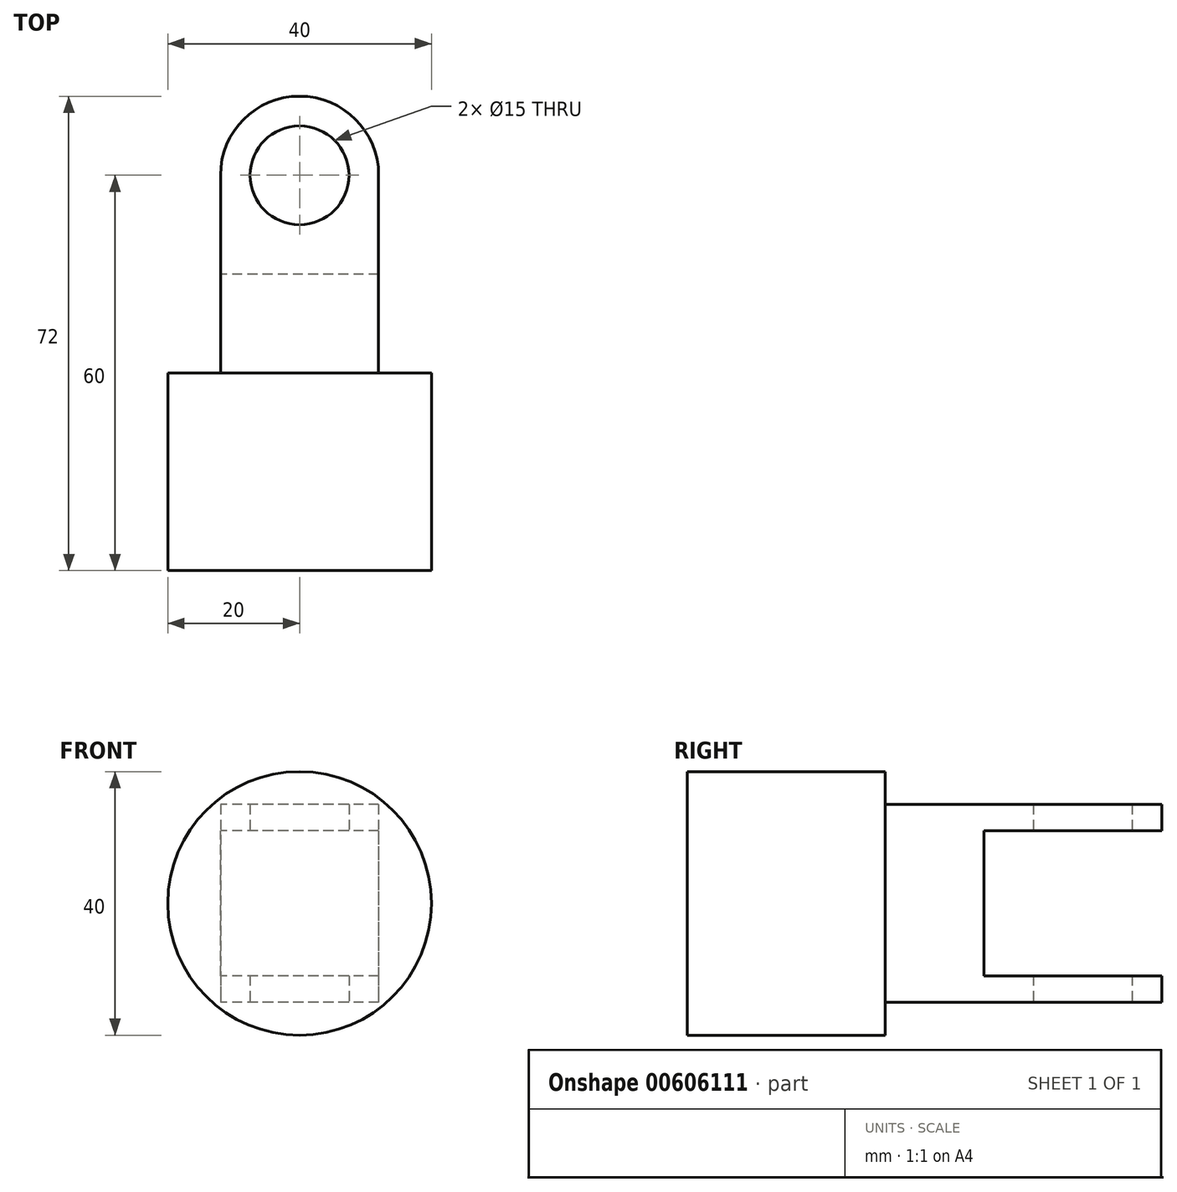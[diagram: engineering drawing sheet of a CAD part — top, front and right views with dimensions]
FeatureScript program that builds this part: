
annotation { "Feature Type Name" : "Feature", "Feature Type Description" : "" }
export const myFeature = defineFeature(function(context is Context, id is Id, definition is map)
    precondition{}
    {
        {
            var Q0;
            Q0=qCreatedBy(makeId("Top.planeOp"),FACE);
            var sketch = newSketch(context, id + "F0", { "sketchPlane" : qUnion([Q0])});
            skLineSegment(sketch, "E0.bottom", {"start": v(12, 15) * mm, "end": v(-12, 15) * mm});
            skLineSegment(sketch, "E0.top", {"start": v(12, -15) * mm, "end": v(-12, -15) * mm});
            skLineSegment(sketch, "E0.left", {"start": v(12, 15) * mm, "end": v(12, -15) * mm});
            skLineSegment(sketch, "E0.right", {"start": v(-12, 15) * mm, "end": v(-12, -15) * mm});
            skPoint(sketch, "E0.middle", {"position": v(0, 0) * mm});
            skCircle(sketch, "E1", {"center": v(0, 15) * mm, "radius": 12 * mm});
            skCircle(sketch, "E2", {"center": v(0, 15) * mm, "radius": 7.5 * mm});
            skSolve(sketch);
        }
        {
            var Q0;
            {var subQ1=sQuery(id+"F0.wireOp",EDGE,"E0.bottom");var subQ3=sQuery(id+"F0.wireOp",EDGE,"E2");var subQ4=makeQuery(id+"F0.imprint","INTERSECT",VERTEX,{"disambiguationData":[OD(0.0)],"derivedFrom":[subQ1,subQ3]});Q0=makeQuery(id+"F0.imprint","IMPRINT",FACE,{"disambiguationData":[TD([[makeQuery(id+"F0.imprint","IMPRINT",EDGE,{"disambiguationData":[TD([[subQ4,-1.0]])],"derivedFrom":subQ3}),-1.0]])]});}
            var Q1;
            {var subQ1=sQuery(id+"F0.wireOp",EDGE,"E0.bottom");var subQ3=sQuery(id+"F0.wireOp",EDGE,"E2");var subQ4=makeQuery(id+"F0.imprint","INTERSECT",VERTEX,{"disambiguationData":[OD(0.0)],"derivedFrom":[subQ1,subQ3]});Q1=makeQuery(id+"F0.imprint","IMPRINT",FACE,{"disambiguationData":[TD([[makeQuery(id+"F0.imprint","IMPRINT",EDGE,{"disambiguationData":[TD([[subQ4,1.0]])],"derivedFrom":subQ3}),-1.0]])]});}
            var Q2;
            Q2=makeQuery(id+"F0.imprint","IMPRINT",FACE,{"disambiguationData":[TD([[makeQuery(id+"F0.imprint","IMPRINT",EDGE,{"derivedFrom":sQuery(id+"F0.wireOp",EDGE,"E0.top")}),-1.0]])]});
            extrude(context, id + "F1", {"entities" : qUnion([Q0, Q1, Q2]), "depth" : 30 * mm, "offsetDistance" : 25.4 * mm});
        }
        {
            var Q0;
            Q0=makeQuery(id+"F1.opExtrude","SWEPT_FACE",FACE,{"disambiguationData":[OSD([sQuery(id+"F0.wireOp",EDGE,"E0.top")])]});
            var sketch = newSketch(context, id + "F2", { "sketchPlane" : qUnion([Q0])});
            skCircle(sketch, "E3", {"center": v(0, 15) * mm, "radius": 20 * mm});
            skPoint(sketch, "E3.centerSnap0", {"position": v(12, 15) * mm});
            skSolve(sketch);
        }
        {
            var Q0;
            Q0=makeQuery(id+"F2.imprint","IMPRINT",FACE,{"disambiguationData":[TD([[makeQuery(id+"F2.imprint","IMPRINT",EDGE,{"derivedFrom":sQuery(id+"F2.wireOp",EDGE,"E3")}),1.0]])]});
            var Q1;
            {var subQ0=sQuery(id+"F0.wireOp",EDGE,"E0.top");Q1=makeQuery(id+"F2.imprint","IMPRINT",FACE,{"disambiguationData":[TD([[makeQuery(id+"F2.imprint","IMPRINT",EDGE,{"derivedFrom":makeQuery(id+"F1.opExtrude","CAP_EDGE",EDGE,{"disambiguationData":[OSD([subQ0])],"isStart":true})}),-1.0]])]});}
            extrude(context, id + "F3", {"entities" : qUnion([Q0, Q1]), "operationType" : NewBodyOperationType.ADD, "depth" : 30 * mm, "offsetDistance" : 25.4 * mm});
        }
        {
            var Q0;
            Q0=makeQuery(id+"F1.opExtrude","SWEPT_FACE",FACE,{"disambiguationData":[OSD([sQuery(id+"F0.wireOp",EDGE,"E0.right")])]});
            var sketch = newSketch(context, id + "F4", { "sketchPlane" : qUnion([Q0])});
            skLineSegment(sketch, "E4.bottom", {"start": v(0, 4) * mm, "end": v(-30, 4) * mm});
            skLineSegment(sketch, "E4.top", {"start": v(0, 26) * mm, "end": v(-30, 26) * mm});
            skLineSegment(sketch, "E4.left", {"start": v(0, 4) * mm, "end": v(0, 26) * mm});
            skLineSegment(sketch, "E4.right", {"start": v(-30, 4) * mm, "end": v(-30, 26) * mm});
            skPoint(sketch, "E4.middle", {"position": v(-15, 15) * mm});
            skSolve(sketch);
        }
        {
            var Q0;
            {var subQ0=sQuery(id+"F4.wireOp",EDGE,"E4.right");Q0=makeQuery(id+"F4.imprint","IMPRINT",FACE,{"disambiguationData":[TD([[makeQuery(id+"F4.imprint","IMPRINT",EDGE,{"derivedFrom":subQ0}),-1.0]])]});}
            var Q1;
            {var subQ0=sQuery(id+"F4.wireOp",EDGE,"E4.left");Q1=makeQuery(id+"F4.imprint","IMPRINT",FACE,{"disambiguationData":[TD([[makeQuery(id+"F4.imprint","IMPRINT",EDGE,{"derivedFrom":subQ0}),1.0]])]});}
            extrude(context, id + "F5", {"entities" : qUnion([Q0, Q1]), "operationType" : NewBodyOperationType.REMOVE, "oppositeDirection" : true, "depth" : 25.4 * mm, "offsetDistance" : 25.4 * mm});
        }
    });
